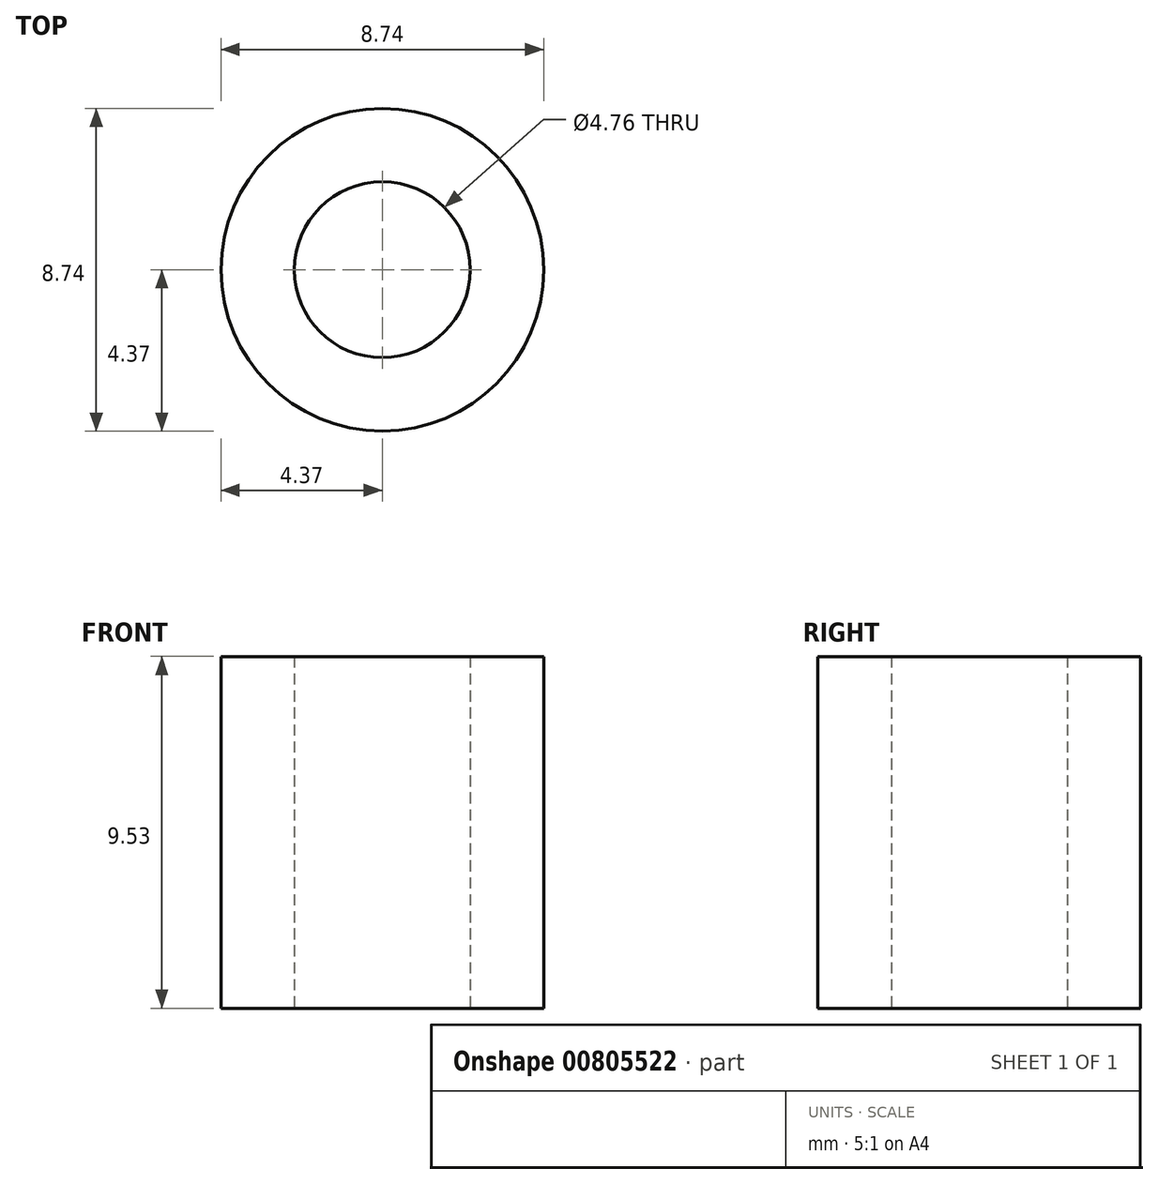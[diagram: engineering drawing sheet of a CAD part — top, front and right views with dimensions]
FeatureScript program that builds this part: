
annotation { "Feature Type Name" : "Feature", "Feature Type Description" : "" }
export const myFeature = defineFeature(function(context is Context, id is Id, definition is map)
    precondition{}
    {
        {
            var Q0;
            Q0=qCreatedBy(makeId("Top.planeOp"),FACE);
            var sketch = newSketch(context, id + "F0", { "sketchPlane" : qUnion([Q0])});
            skCircle(sketch, "E0", {"center": v(0, 0) * mm, "radius": 2.38 * mm});
            skCircle(sketch, "E1", {"center": v(0, 0) * mm, "radius": 4.37 * mm});
            skSolve(sketch);
        }
        {
            var Q0;
            Q0=makeQuery(id+"F0.imprint","IMPRINT",FACE,{"disambiguationData":[TD([[makeQuery(id+"F0.imprint","IMPRINT",EDGE,{"derivedFrom":sQuery(id+"F0.wireOp",EDGE,"E0")}),-1.0]])]});
            extrude(context, id + "F1", {"entities" : qUnion([Q0]), "depth" : 9.53 * mm, "offsetDistance" : 25 * mm});
        }
    });
